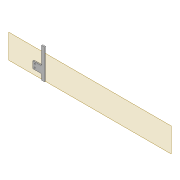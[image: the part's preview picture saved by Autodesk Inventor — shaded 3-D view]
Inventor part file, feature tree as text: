
AUTODESK INVENTOR PART (.ipt)
format: ipt  version: 2022 (Build 260153000, 153)  size: 505,344 bytes
history: native  units: mm
features: sketch x9, projected_geometry x9, extrude x8, fillet x2, shell x1, plane x1, chamfer x1
ambient origin geometry x8: Origin, YZ Plane, XZ Plane, XY Plane, X Axis, Y Axis, Z Axis, Center Point
bodies: Solid1 (feature_tree)
feature tree (31):
  extrude  "Extrusion1"  Depth=2.0mm
  shell  "Shell1"  Thickness=2.0mm
  extrude  "Extrusion8"  Depth=2.0mm
  extrude  "Extrusion3"  Depth=10.0mm TaperAngle=0.0deg
  extrude  "Extrusion4"  Depth=2.0mm
  fillet  "Fillet1"  Radius=5.0mm
  sketch  "Sketch10"  dims[d22=2.0mm d23=0.0mm d31=2.0mm d32=5.0mm]
  extrude  "Extrusion5"  Depth=2.5mm
  plane  "Work Plane2"
  extrude  "Extrusion9"  Depth=5.0mm
  fillet  "Fillet2"  Radius=2.5mm
  extrude  "Extrusion10"  Depth=2.0mm
  chamfer  "Chamfer1"  Distance=2.0mm
  extrude  "Extrusion12"  Depth=12.0mm
  sketch  "Sketch29"  dims[d66=3.0mm d67=12.0mm]
  sketch  "Sketch30"  dims[d68=5.0mm d69=15.0mm d70=12.0mm d71=3.05mm d72=10.0mm d73=0.0mm d74=2.0mm d75=100.0mm d76=20.0mm d77=0.5mm d78=10.0mm d79=0.0mm d82=3.0mm d83=2.0mm d84=45.0deg d85=1.0mm d86=1.0mm d87=1.0mm d88=1.0mm d89=1.0mm d91=1.0mm d92=10.0mm d93=0.0mm]
  sketch  "Sketch3"  dims[d0=2.0mm d1=0.0mm d2=4.0mm d7=2.0mm]
  sketch  "Sketch8"  dims[d8=2.0mm d9=5.9mm]
  sketch  "Sketch9"  dims[d13=10.0mm d14=0.0mm d16=10.0mm d17=0.0mm]
  projected_geometry  "Projected Loop4"
  projected_geometry  "Projected Loop10"
  sketch  "Sketch24"  dims[d34=1.6mm d35=2.5mm]
  projected_geometry  "Projected Loop11"
  projected_geometry  "Projected Loop12"
  projected_geometry  "Projected Loop13"
  sketch  "Sketch26"  dims[d37=5.0mm d38=1.6mm d40=2.5mm]
  projected_geometry  "Projected Loop14"
  sketch  "Sketch28"  dims[d62=80.0mm d63=6.0mm d64=2.0mm d65=0.0mm]
  projected_geometry  "Project Cut Edges1"
  projected_geometry  "Project Cut Edges2"
  projected_geometry  "Project Cut Edges3"
